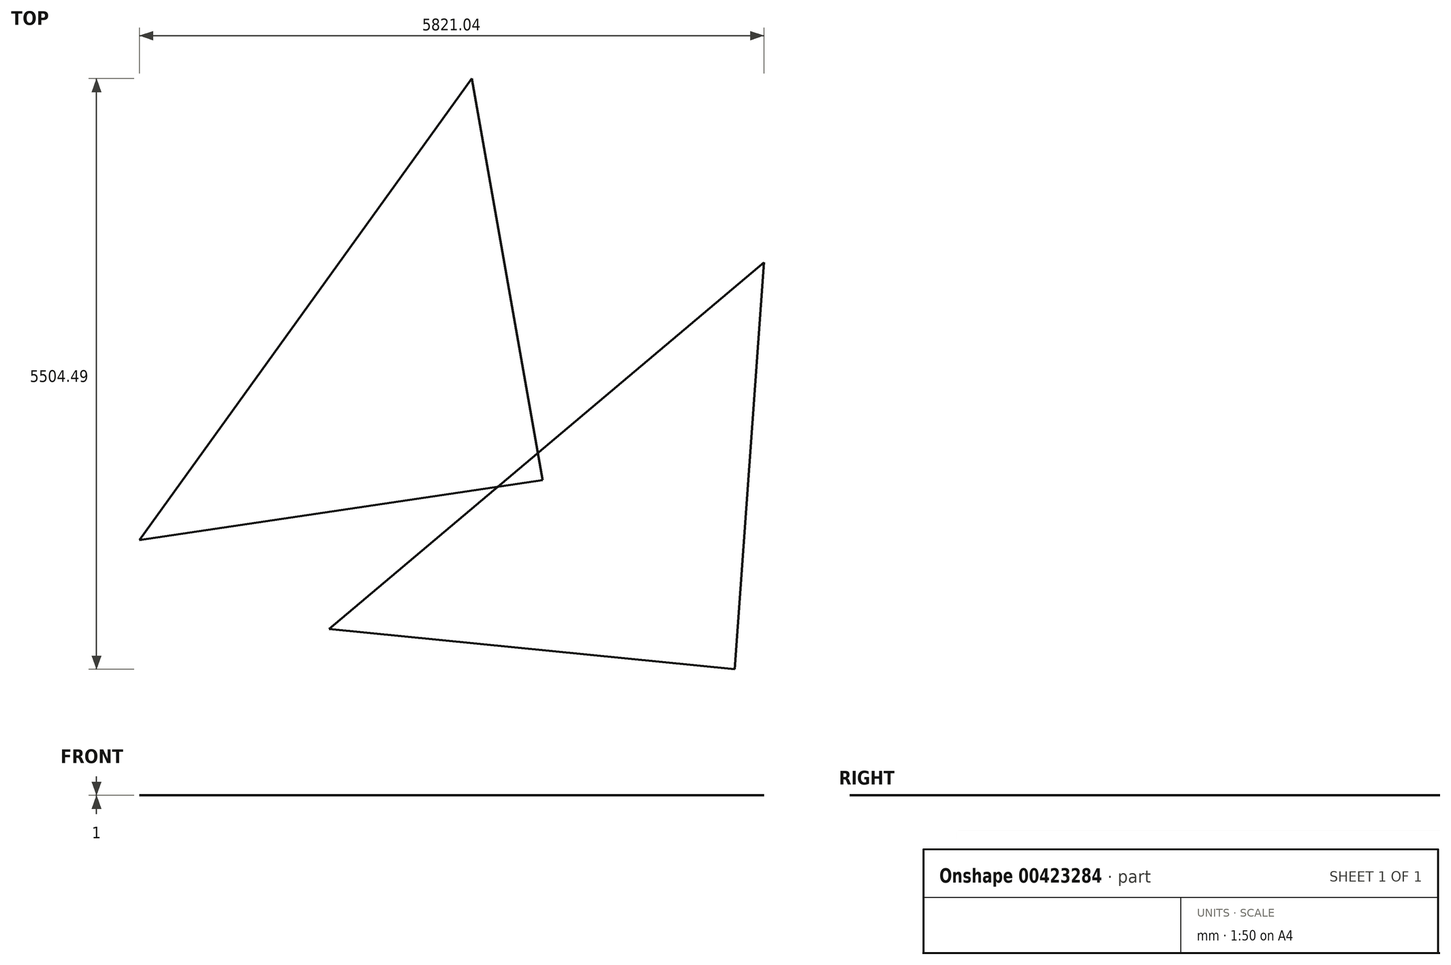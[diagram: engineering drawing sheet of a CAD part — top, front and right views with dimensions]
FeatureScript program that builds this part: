
annotation { "Feature Type Name" : "Feature", "Feature Type Description" : "" }
export const myFeature = defineFeature(function(context is Context, id is Id, definition is map)
    precondition{}
    {
        {
            var Q0;
            Q0=qCreatedBy(makeId("Top.planeOp"),FACE);
            var sketch = newSketch(context, id + "F0", { "sketchPlane" : qUnion([Q0])});
            skLineSegment(sketch, "E0", {"start": v(0, 0) * mm, "end": v(-4850, 0) * mm});
            skLineSegment(sketch, "E1", {"start": v(-4850, 0) * mm, "end": v(-4850, 1700) * mm});
            skLineSegment(sketch, "E2", {"start": v(-4850, 1700) * mm, "end": v(-8250, 1700) * mm});
            skLineSegment(sketch, "E3", {"start": v(0, 0) * mm, "end": v(0, 5000) * mm});
            skLineSegment(sketch, "E4", {"start": v(0, 5000) * mm, "end": v(-2800, 5000) * mm});
            skLineSegment(sketch, "E5", {"start": v(-2800, 5000) * mm, "end": v(-2800, 8045.54) * mm});
            skLineSegment(sketch, "E6", {"start": v(-466.34, 489.25) * mm, "end": v(-1625.2, 3897.63) * mm});
            skLineSegment(sketch, "E7", {"start": v(-1625.2, 3897.63) * mm, "end": v(-3997.51, 1189.85) * mm});
            skLineSegment(sketch, "E8", {"start": v(-3997.51, 1189.85) * mm, "end": v(-466.34, 489.25) * mm});
            skPoint(sketch, "E9", {"position": v(-4850, 900) * mm});
            skPoint(sketch, "E10", {"position": v(-5650, 1700) * mm});
            skPoint(sketch, "E11", {"position": v(-2800, 6016.08) * mm});
            skPoint(sketch, "E12", {"position": v(-2800, 7700) * mm});
            skLineSegment(sketch, "E13", {"start": v(-6374.1, 1824.68) * mm, "end": v(-3276.85, 6125.5) * mm});
            skLineSegment(sketch, "E14", {"start": v(-3276.85, 6125.5) * mm, "end": v(-2615.42, 2383.5) * mm});
            skLineSegment(sketch, "E15", {"start": v(-2615.42, 2383.5) * mm, "end": v(-6374.1, 1824.68) * mm});
            skPoint(sketch, "E16", {"position": v(-2000, 5000) * mm});
            skPoint(sketch, "E17", {"position": v(-300, 0) * mm});
            skPoint(sketch, "E18", {"position": v(-1150, 0) * mm});
            skLineSegment(sketch, "E19", {"start": v(-4850, 900) * mm, "end": v(-1045.77, 2193.44) * mm, "construction": true});
            skPoint(sketch, "E20", {"position": v(0, 500) * mm});
            skPoint(sketch, "E21", {"position": v(-6550, 1700) * mm});
            skLineSegment(sketch, "E22", {"start": v(-2800, 7700) * mm, "end": v(-3276.85, 6125.5) * mm});
            skPoint(sketch, "E23", {"position": v(-2946.13, 4254.5) * mm});
            skPoint(sketch, "E24", {"position": v(-4825.48, 3975.09) * mm});
            skPoint(sketch, "E25", {"position": v(-4494.76, 2104.1) * mm});
            skLineSegment(sketch, "E26", {"start": v(-6550, 1700) * mm, "end": v(-6374.1, 1824.68) * mm});
            skLineSegment(sketch, "E27", {"start": v(-2615.42, 2383.5) * mm, "end": v(0, 500) * mm});
            skSolve(sketch);
        }
        {
            var Q0;
            {var subQ5=sQuery(id+"F0.wireOp",EDGE,"E13");Q0=makeQuery(id+"F0.imprint","IMPRINT",FACE,{"disambiguationData":[TD([[makeQuery(id+"F0.imprint","IMPRINT",EDGE,{"derivedFrom":subQ5}),-1.0]])]});}
            var Q1;
            {var subQ0=sQuery(id+"F0.wireOp",EDGE,"E14");var subQ1=sQuery(id+"F0.wireOp",EDGE,"E7");var subQ2=makeQuery(id+"F0.imprint","INTERSECT",VERTEX,{"derivedFrom":[subQ1,subQ0]});Q1=makeQuery(id+"F0.imprint","IMPRINT",FACE,{"disambiguationData":[TD([[makeQuery(id+"F0.imprint","IMPRINT",EDGE,{"disambiguationData":[TD([[subQ2,-1.0]])],"derivedFrom":subQ1}),1.0]])]});}
            extrude(context, id + "F1", {"entities" : qUnion([Q0, Q1]), "depth" : 1 * mm});
        }
        {
            var Q0;
            Q0=qCreatedBy(makeId("Top.planeOp"),FACE);
            var sketch = newSketch(context, id + "F2", { "sketchPlane" : qUnion([Q0])});
            skLineSegment(sketch, "E28", {"start": v(-4605.11, 995.1) * mm, "end": v(-553.06, 4411.37) * mm});
            skLineSegment(sketch, "E29", {"start": v(-553.06, 4411.37) * mm, "end": v(-823.57, 621.01) * mm});
            skLineSegment(sketch, "E30", {"start": v(-823.57, 621.01) * mm, "end": v(-4605.11, 995.1) * mm});
            skLineSegment(sketch, "E31", {"start": v(-823.57, 621.01) * mm, "end": v(-300, 0) * mm});
            skPoint(sketch, "E32", {"position": v(-2579.09, 2703.24) * mm});
            skLineSegment(sketch, "E33", {"start": v(-553.06, 4411.37) * mm, "end": v(-200, 5000) * mm});
            skPoint(sketch, "E34", {"position": v(-2714.34, 808.06) * mm});
            skPoint(sketch, "E35", {"position": v(-688.32, 2516.2) * mm});
            skLineSegment(sketch, "E36", {"start": v(-4605.11, 995.1) * mm, "end": v(-4850, 900) * mm});
            skSolve(sketch);
        }
        {
            var Q0;
            Q0 = qSketchRegion(id + "F2", true);
            extrude(context, id + "F3", {"entities" : qUnion([Q0]), "depth" : 1 * mm});
        }
    });
